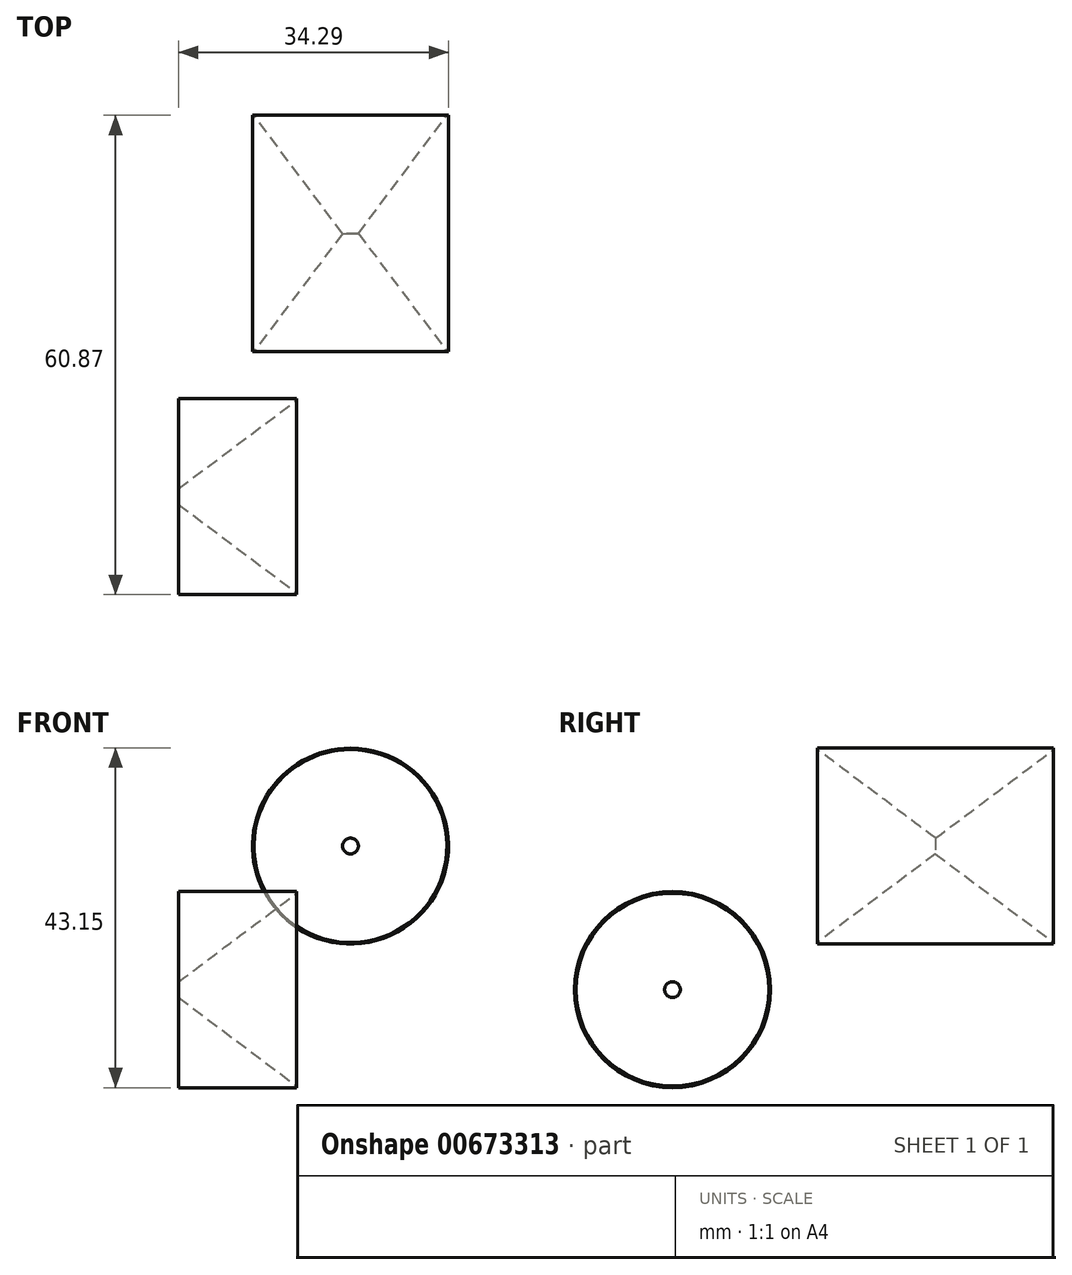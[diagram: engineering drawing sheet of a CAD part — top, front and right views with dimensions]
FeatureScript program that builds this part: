
annotation { "Feature Type Name" : "Feature", "Feature Type Description" : "" }
export const myFeature = defineFeature(function(context is Context, id is Id, definition is map)
    precondition{}
    {
        {
            var Q0;
            Q0=qCreatedBy(makeId("Right.planeOp"),FACE);
            var sketch = newSketch(context, id + "F0", { "sketchPlane" : qUnion([Q0])});
            skLineSegment(sketch, "E0", {"start": v(48.12, 11.1) * mm, "end": v(13.33, 11.1) * mm, "construction": true});
            skLineSegment(sketch, "E1", {"start": v(33.42, 12.1) * mm, "end": v(48.42, 23.35) * mm});
            skLineSegment(sketch, "E2", {"start": v(48.42, 23.35) * mm, "end": v(48.42, 23.55) * mm});
            skLineSegment(sketch, "E3", {"start": v(48.42, 23.55) * mm, "end": v(18.42, 23.55) * mm});
            skLineSegment(sketch, "E4", {"start": v(18.42, 23.55) * mm, "end": v(18.42, 23.35) * mm});
            skLineSegment(sketch, "E5", {"start": v(18.42, 23.35) * mm, "end": v(33.42, 12.1) * mm});
            skSolve(sketch);
        }
        {
            var Q0;
            Q0=makeQuery(id+"F0.imprint","IMPRINT",FACE,{"disambiguationData":[TD([[makeQuery(id+"F0.imprint","IMPRINT",EDGE,{"derivedFrom":sQuery(id+"F0.wireOp",EDGE,"E1")}),1.0]])]});
            var Q1;
            Q1=sQuery(id+"F0.wireOp",EDGE,"E0");
            revolve(context, id + "F1", {"entities" : qUnion([Q0]), "axis" : qUnion([Q1]), "revolveType" : RevolveType.FULL});
        }
        {
            var Q0;
            Q0=qCreatedBy(makeId("Front.planeOp"),FACE);
            var sketch = newSketch(context, id + "F2", { "sketchPlane" : qUnion([Q0])});
            skLineSegment(sketch, "E6", {"start": v(-21.66, -7.15) * mm, "end": v(-8.38, -7.15) * mm, "construction": true});
            skLineSegment(sketch, "E7", {"start": v(-21.84, 5.3) * mm, "end": v(-6.84, 5.3) * mm});
            skLineSegment(sketch, "E8", {"start": v(-6.84, 5.3) * mm, "end": v(-6.84, 5.1) * mm});
            skLineSegment(sketch, "E9", {"start": v(-6.84, 5.1) * mm, "end": v(-21.84, -6.15) * mm});
            skLineSegment(sketch, "E10", {"start": v(-21.84, -6.15) * mm, "end": v(-21.84, 5.3) * mm});
            skSolve(sketch);
        }
        {
            var Q0;
            Q0=makeQuery(id+"F2.imprint","IMPRINT",FACE,{"disambiguationData":[TD([[makeQuery(id+"F2.imprint","IMPRINT",EDGE,{"derivedFrom":sQuery(id+"F2.wireOp",EDGE,"E7")}),-1.0]])]});
            var Q1;
            Q1=sQuery(id+"F2.wireOp",EDGE,"E6");
            revolve(context, id + "F3", {"entities" : qUnion([Q0]), "axis" : qUnion([Q1]), "revolveType" : RevolveType.FULL});
        }
    });
